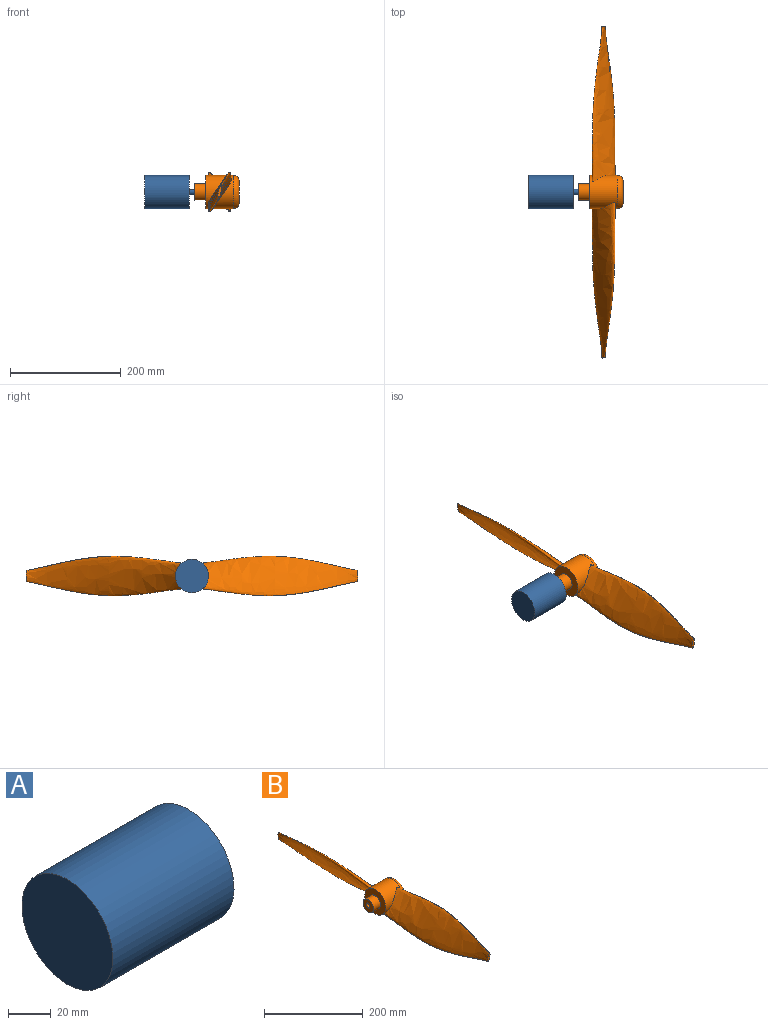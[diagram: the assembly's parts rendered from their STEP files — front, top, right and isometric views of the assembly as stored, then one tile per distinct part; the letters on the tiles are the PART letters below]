
ASSEMBLY  parts=2 mates=1
PART A: 5 faces, bbox 95x60x60 mm
  f0: plane 60x60mm, normal (-1,0,0), area 2827.4mm2, adj f4
  f1: plane 10x10mm, normal (1,0,0), area 78.5mm2, adj f2
  f2: cylinder r=5mm len=15mm, axis (-1,0,0), area 471.2mm2, adj f1,f3
  f3: plane 60x60mm, normal (1,0,0), area 2748.9mm2, adj f2,f4
  f4: cylinder r=30mm len=80mm, axis (-1,0,0), area 15079.6mm2, adj f0,f3
PART B: 15 faces, bbox 80x600x95 mm
  f0: plane 30x30mm, normal (-1,0,0), area 624.5mm2, adj f1,f6,f7,f8,f9
  f1: cylinder r=15mm len=30mm, axis (-1,0,0), area 1885mm2, adj f0,f4
  f2: plane 40x40mm, normal (1,0,0), area 1256.6mm2, adj f5
  f3: cylinder r=30mm len=60mm, axis (-1,0,0), area 8042.7mm2, adj f4,f5,f11,f13
  f4: plane 60x60mm, normal (-1,0,0), area 2120.6mm2, adj f1,f3
  f5: torus R=20mm, axis (-1,0,0), area 2602.2mm2, adj f2,f3
  f6: plane 20x2.7mm, normal (0.02,0,-1), area 47mm2, adj f0,f7,f9,f10
  f7: plane 20.01x2.36mm, normal (0.02,-1,0), area 40.7mm2, adj f0,f6,f8,f10
  f8: cone r=5mm half-angle=1deg, axis (1,0,0), area 603.1mm2, adj f0,f7,f9,f10
  f9: plane 20.01x2.36mm, normal (0.02,1,0), area 40.7mm2, adj f0,f6,f8,f10
  f10: plane 12.6x10.7mm, normal (-1,0,0), area 95.2mm2, adj f6,f7,f8,f9
  f11: bspline ~300x95.03mm, area 35764.1mm2, adj f3,f12
  f12: plane 19.74x6.03mm, normal (0,1,0), area 78.5mm2, adj f11
  f13: bspline ~300x95.03mm, area 35764.1mm2, adj f3,f14
  f14: plane 19.74x6.03mm, normal (0,-1,0), area 78.5mm2, adj f13
PLACE A t=(-169.37,-52.31,34.01)mm
PLACE B t=(-34.37,-52.31,34.01)mm
MATE revolute B.f1 <-> A.f2  axis (-1,0,0) through (-59.37,-52.31,34.01)mm
